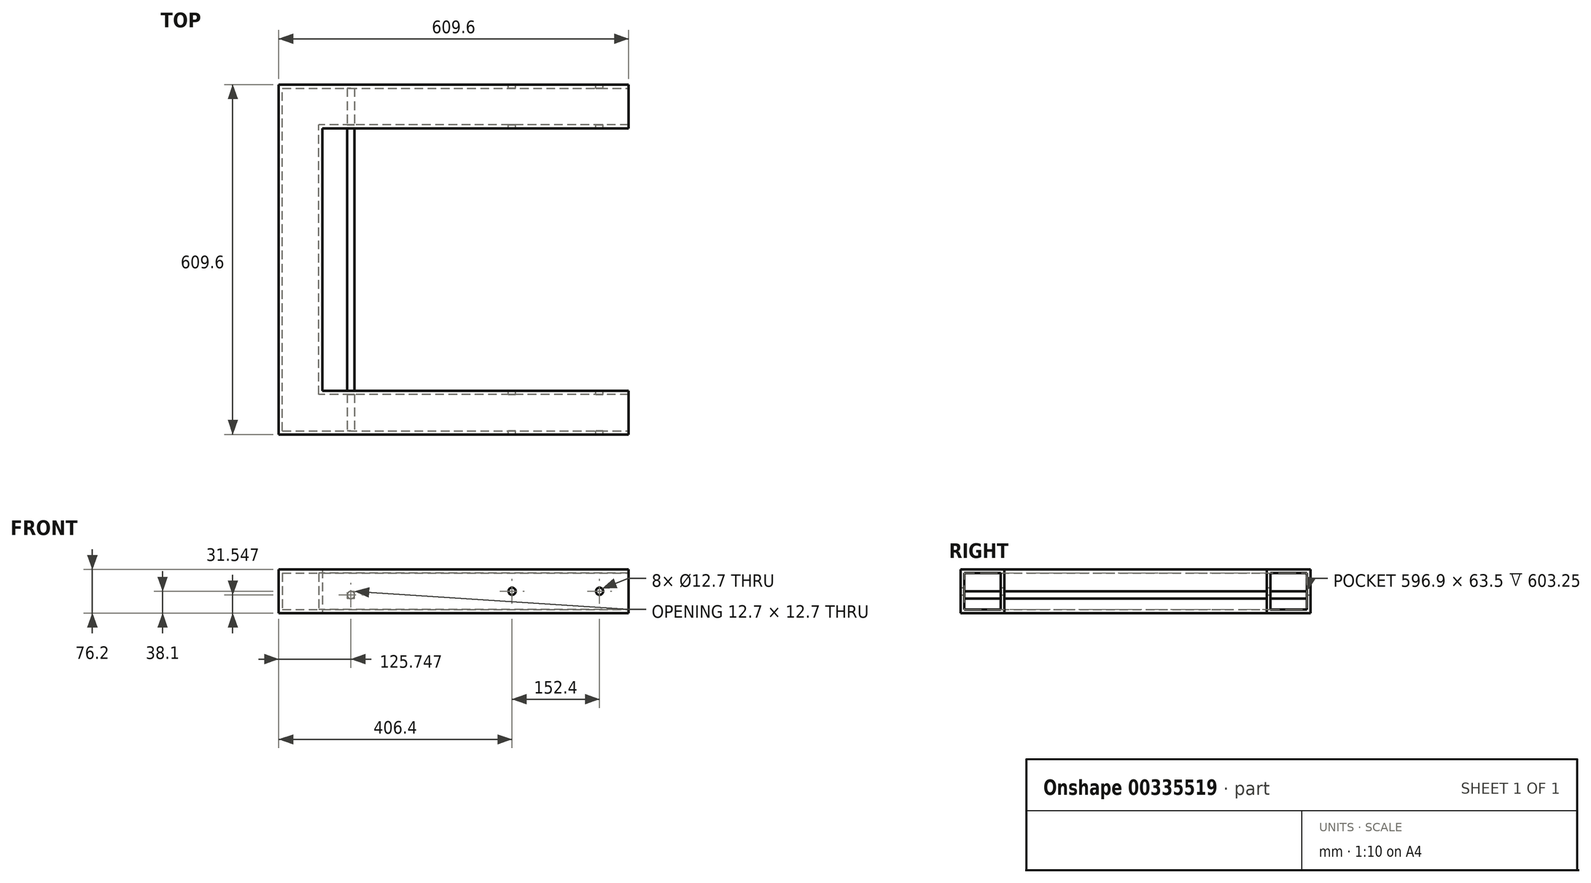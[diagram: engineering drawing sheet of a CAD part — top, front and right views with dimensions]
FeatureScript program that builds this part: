
annotation { "Feature Type Name" : "Feature", "Feature Type Description" : "" }
export const myFeature = defineFeature(function(context is Context, id is Id, definition is map)
    precondition{}
    {
        {
            var Q0;
            Q0=qCreatedBy(makeId("Top.planeOp"),FACE);
            var sketch = newSketch(context, id + "F0", { "sketchPlane" : qUnion([Q0])});
            skLineSegment(sketch, "E0.bottom", {"start": v(-304.8, -304.8) * mm, "end": v(304.8, -304.8) * mm});
            skLineSegment(sketch, "E0.top", {"start": v(-304.8, 304.8) * mm, "end": v(304.8, 304.8) * mm});
            skLineSegment(sketch, "E0.left", {"start": v(-304.8, -304.8) * mm, "end": v(-304.8, 304.8) * mm});
            skLineSegment(sketch, "E0.right", {"start": v(304.8, -304.8) * mm, "end": v(304.8, -228.6) * mm});
            skPoint(sketch, "E0.middle", {"position": v(0, 0) * mm});
            skLineSegment(sketch, "E1.bottom", {"start": v(304.8, -228.6) * mm, "end": v(-228.6, -228.6) * mm});
            skLineSegment(sketch, "E1.top", {"start": v(304.8, 228.6) * mm, "end": v(-228.6, 228.6) * mm});
            skLineSegment(sketch, "E1.right", {"start": v(-228.6, -228.6) * mm, "end": v(-228.6, 228.6) * mm});
            skLineSegment(sketch, "E2.trimOffspring", {"start": v(304.8, 228.6) * mm, "end": v(304.8, 304.8) * mm});
            skSolve(sketch);
        }
        {
            var Q0;
            Q0=makeQuery(id+"F0.imprint","IMPRINT",FACE,{"disambiguationData":[TD([[makeQuery(id+"F0.imprint","IMPRINT",EDGE,{"derivedFrom":sQuery(id+"F0.wireOp",EDGE,"E0.bottom")}),1.0]])]});
            extrude(context, id + "F1", {"entities" : qUnion([Q0]), "depth" : 76.2 * mm});
        }
        {
            var Q0;
            Q0=makeQuery(id+"F1.opExtrude","SWEPT_FACE",FACE,{"disambiguationData":[OSD([sQuery(id+"F0.wireOp",EDGE,"E0.right")])]});
            var Q1;
            Q1=makeQuery(id+"F1.opExtrude","SWEPT_FACE",FACE,{"disambiguationData":[OSD([sQuery(id+"F0.wireOp",EDGE,"E2.trimOffspring")])]});
            shell(context, id + "F2", {"entities" : qUnion([Q0, Q1]), "thickness" : 6.35 * mm});
        }
        {
            var Q0;
            Q0=makeQuery(id+"F1.opExtrude","SWEPT_FACE",FACE,{"disambiguationData":[OSD([sQuery(id+"F0.wireOp",EDGE,"E0.bottom")])]});
            var sketch = newSketch(context, id + "F3", { "sketchPlane" : qUnion([Q0])});
            skCircle(sketch, "E3", {"center": v(-179.05, 31.55) * mm, "radius": 6.35 * mm});
            skSolve(sketch);
        }
        {
            var Q0;
            Q0=makeQuery(id+"F3.imprint","IMPRINT",FACE,{"disambiguationData":[TD([[makeQuery(id+"F3.imprint","IMPRINT",EDGE,{"derivedFrom":sQuery(id+"F3.wireOp",EDGE,"E3")}),1.0]])]});
            var Q1;
            Q1=makeQuery(id+"F1.opExtrude","SWEPT_FACE",FACE,{"disambiguationData":[OSD([sQuery(id+"F0.wireOp",EDGE,"E0.top")])]});
            extrude(context, id + "F4", {"entities" : qUnion([Q0]), "operationType" : NewBodyOperationType.ADD, "oppositeDirection" : true, "depth" : 609.6 * mm});
        }
        {
            var Q0;
            Q0=makeQuery(id+"F1.opExtrude","SWEPT_FACE",FACE,{"disambiguationData":[OSD([sQuery(id+"F0.wireOp",EDGE,"E0.top")])]});
            var sketch = newSketch(context, id + "F5", { "sketchPlane" : qUnion([Q0])});
            skPoint(sketch, "E4", {"position": v(-254, 38.1) * mm});
            skPoint(sketch, "E5", {"position": v(-101.6, 38.1) * mm});
            skSolve(sketch);
        }
        {
            var Q0;
            Q0=sQuery(id+"F5.wireOp",VERTEX,"E4");
            var Q1;
            Q1=sQuery(id+"F5.wireOp",VERTEX,"E5");
            var Q2;
            Q2=makeQuery(id+"F1.opExtrude","SWEPT_BODY",BODY,{"disambiguationData":[OSD([sQuery(id+"F0.wireOp",EDGE,"E0.bottom"),sQuery(id+"F0.wireOp",EDGE,"E0.top"),sQuery(id+"F0.wireOp",EDGE,"E0.left"),sQuery(id+"F0.wireOp",EDGE,"E0.right"),sQuery(id+"F0.wireOp",EDGE,"E1.bottom"),sQuery(id+"F0.wireOp",EDGE,"E1.top"),sQuery(id+"F0.wireOp",EDGE,"E1.right"),sQuery(id+"F0.wireOp",EDGE,"E2.trimOffspring")])]});
            hole(context, id + "F6", {"style" : HoleStyle.SIMPLE, "endStyle" : HoleEndStyle.THROUGH, "holeDiameter" : 12.7 * mm, "tappedDepth" : 12.7 * mm, "tapClearance" : 3, "locations" : qUnion([Q0, Q1]), "scope" : qUnion([Q2])});
        }
    });
